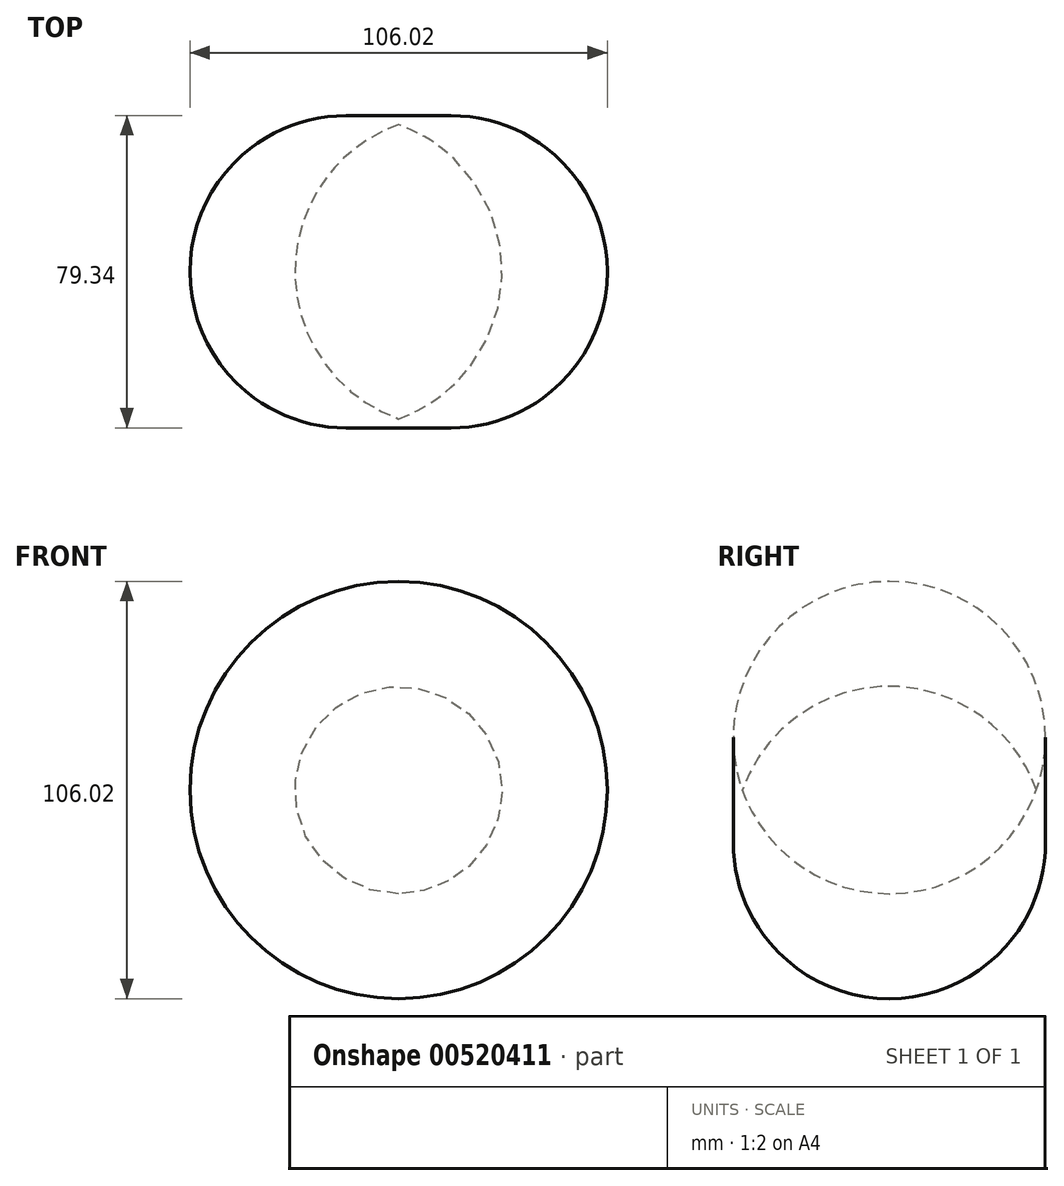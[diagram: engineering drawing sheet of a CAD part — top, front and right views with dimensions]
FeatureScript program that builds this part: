
annotation { "Feature Type Name" : "Feature", "Feature Type Description" : "" }
export const myFeature = defineFeature(function(context is Context, id is Id, definition is map)
    precondition{}
    {
        {
            var Q0;
            Q0=qCreatedBy(makeId("Top.planeOp"),FACE);
            var sketch = newSketch(context, id + "F0", { "sketchPlane" : qUnion([Q0])});
            skLineSegment(sketch, "E0", {"start": v(0, 77.2) * mm, "end": v(0, -78.37) * mm});
            skArc(sketch, "E1", {"start": v(0, 47.54) * mm, "mid": v(-53, 10.17) * mm, "end": v(0, -27.19) * mm});
            skPoint(sketch, "E2.orphan", {"position": v(25, 0) * mm});
            skSolve(sketch);
        }
        {
            var Q0;
            {var subQ0=sQuery(id+"F0.wireOp",EDGE,"E1");Q0=makeQuery(id+"F0.imprint","IMPRINT",FACE,{"disambiguationData":[TD([[makeQuery(id+"F0.imprint","IMPRINT",EDGE,{"derivedFrom":subQ0}),1.0]])]});}
            var Q1;
            Q1=sQuery(id+"F0.wireOp",EDGE,"E0");
            revolve(context, id + "F1", {"entities" : qUnion([Q0]), "axis" : qUnion([Q1]), "revolveType" : RevolveType.FULL});
        }
    });
